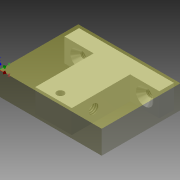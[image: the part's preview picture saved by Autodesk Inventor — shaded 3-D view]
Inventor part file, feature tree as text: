
AUTODESK INVENTOR PART (.ipt)
format: ipt  version: 2015 SP1 (Build 190203100, 203)  size: 332,288 bytes
history: native  units: in
note: dims shown in document units (in); Inventor stores cm internally (conversion verified against a paired STEP export)
features: extrude x3, hole x3, sketch x3, pattern_linear x1, projected_geometry x1
ambient origin geometry x8: Origin, YZ Plane, XZ Plane, XY Plane, X Axis, Y Axis, Z Axis, Center Point
bodies: Solid1 (feature_tree)
feature tree (11):
  extrude  "Extrusion1"  Depth=0.3937in TaperAngle=0.0deg
  hole  "Hole1"  [1 undecoded]
  hole  "Hole2"  [1 undecoded]
  extrude  "Extrusion4"  Depth=0.315in
  extrude  "Extrusion5"  Depth=0.7874in
  hole  "Hole3"  [1 undecoded]
  pattern_linear  "Rectangular Pattern1"  [2 undecoded]
  sketch  "Sketch1"  dims[d2=0.0in]
  sketch  "Sketch2"  dims[d3=0.0984in d4=0.2411in d5=0.0968in d6=0.2362in d7=0.1575in d8=0.0787in d9=90.0deg d10=0.315in d11=0.8108in]
  projected_geometry  "Projected Loop1"
  sketch  "Sketch4"  dims[d12=0.2953in d13=0.1575in d14=0.1276in d15=0.315in d16=0.1575in d17=0.0787in d18=90.0deg d19=0.4646in d20=0.8108in d26=0.3937in d27=0.0in d28=0.1969in d29=0.3937in d30=0.0in d31=0.1575in d32=0.1969in d33=0.0968in d34=0.2362in d35=0.2362in d36=0.0787in d37=90.0deg d38=0.315in d39=0.8108in d40=0.315in d41=0.7874in d43=0.8858in]
note: 5 required parameter values undecoded (feature->parameter linkage not recoverable at this tier; creation-order binding heuristic only, values carry confidence <= 0.55)
